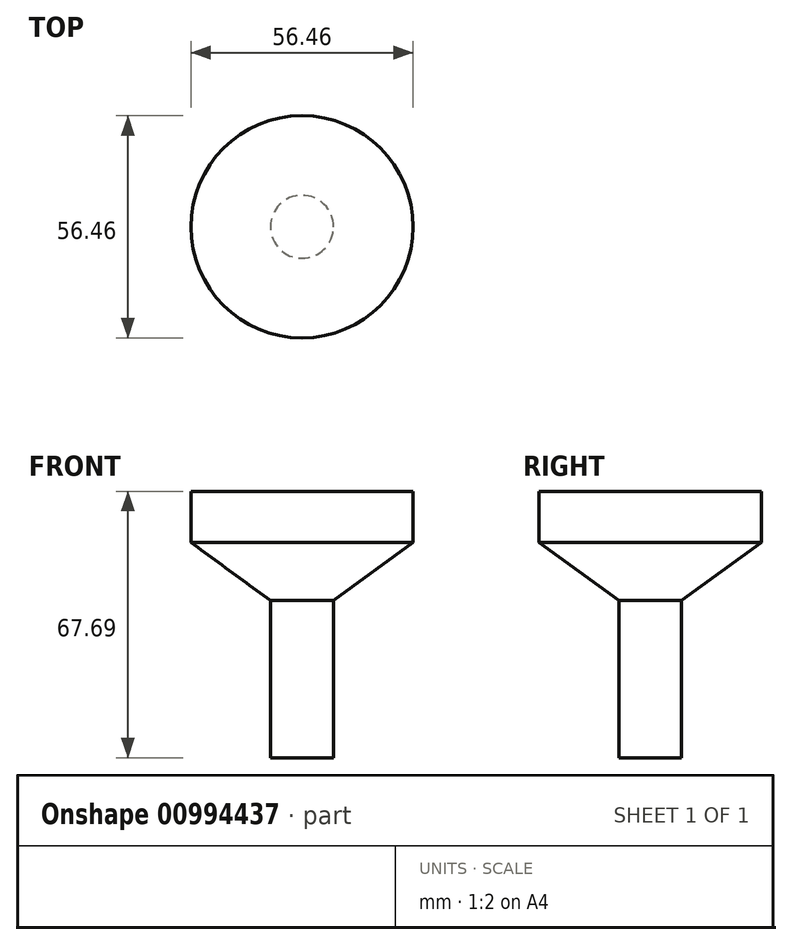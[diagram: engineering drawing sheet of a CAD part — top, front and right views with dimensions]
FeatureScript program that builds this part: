
annotation { "Feature Type Name" : "Feature", "Feature Type Description" : "" }
export const myFeature = defineFeature(function(context is Context, id is Id, definition is map)
    precondition{}
    {
        {
            var Q0;
            Q0=qCreatedBy(makeId("Front.planeOp"),FACE);
            var sketch = newSketch(context, id + "F0", { "sketchPlane" : qUnion([Q0])});
            skLineSegment(sketch, "E0.bottom", {"start": v(0, 20) * mm, "end": v(-8, 20) * mm});
            skLineSegment(sketch, "E0.top", {"start": v(0, -20) * mm, "end": v(-8, -20) * mm});
            skLineSegment(sketch, "E0.right", {"start": v(-8, 20) * mm, "end": v(-8, -20) * mm});
            skPoint(sketch, "E0.middle", {"position": v(0, 0) * mm});
            skLineSegment(sketch, "E1", {"start": v(-8, 20) * mm, "end": v(-28.23, 34.7) * mm});
            skLineSegment(sketch, "E2", {"start": v(-28.23, 34.7) * mm, "end": v(-28.23, 47.7) * mm});
            skLineSegment(sketch, "E3", {"start": v(-28.23, 47.7) * mm, "end": v(0, 47.7) * mm});
            skLineSegment(sketch, "E4", {"start": v(0, -20) * mm, "end": v(0, 47.7) * mm});
            skSolve(sketch);
        }
        {
            var Q0;
            Q0=makeQuery(id+"F0.imprint","IMPRINT",FACE,{"disambiguationData":[TD([[makeQuery(id+"F0.imprint","IMPRINT",EDGE,{"derivedFrom":sQuery(id+"F0.wireOp",EDGE,"E0.bottom")}),-1.0]])]});
            var Q1;
            Q1=makeQuery(id+"F0.imprint","IMPRINT",FACE,{"disambiguationData":[TD([[makeQuery(id+"F0.imprint","IMPRINT",EDGE,{"derivedFrom":sQuery(id+"F0.wireOp",EDGE,"E0.bottom")}),1.0]])]});
            var Q2;
            Q2=sQuery(id+"F0.wireOp",EDGE,"E4");
            revolve(context, id + "F1", {"surfaceOperationType" : NewSurfaceOperationType.NEW, "entities" : qUnion([Q0, Q1]), "axis" : qUnion([Q2]), "revolveType" : RevolveType.FULL});
        }
    });
